# Revit family: Faucet-Bidet-KOHLER-STRAYT-K-37342IN_1
name_source: partatom
category: Plumbing Fixtures
revit_build: Autodesk Revit 2017 (Build: 20160225_1515(x64)
units: mm (PartAtom-declared; Revit-internal decimal feet)

## family parameters
Cut with Voids When Loaded = No
Host = Face
OmniClass Number = 23.31.11.00
OmniClass Title = Faucets
Part Type = Normal
Room Calculation Point = No
Round Connector Dimension = Use Diameter
Shared = No

## types (2) — shared parameters
ADA Compliant = No
Assembly Code = D2010
CW Connection = Yes
Cold Water Inlet = Cold Water Inlet
Date Modified = 05/20/2021
Default Elevation = 36"
Description = STRAY 2 WAY BIB TAP
Drain Included = No
Flow Rate = 0 GPM
HW Connection = No
Handle Clearance = 2 9/16"
Height = 3 1/4"
Hot Water Inlet = Hot Water Inlet
Length = 5 1/16"
Manufacturer = KOHLER Co.
Master Format 2014 Name = Residential Faucets, Supplies, and Trim
MasterFormat 2014 = 22.41.39
Material = Premium Metal Construction
Pressure = 0.00 psi
Product Name = STRAYT
Spout Reach = 5 1/16"
URL = https://www.kohler.co.in
Vent Connection = No
Waste Connection = No
Waste Water Outlet = Waste Water Outlet
WaterSense Certified = No
Width = 2 1/2"
zero-valued in all types: WFU

## per-type parameters (varying)
| type | Finish | Model | Type |
| CP-Polished Chrome | Kohler-Metal-CP-Polished_Chrome | K-37342IN-4-CP | 1 |
| AF-French Gold | Kohler-Metal-AF-Vibrant_French_Gold | K-37342IN-4-AF | 2 |

## geometry (parser evidence)
native form markers: Sweep x5
no freeform markers — native parametric forms only
